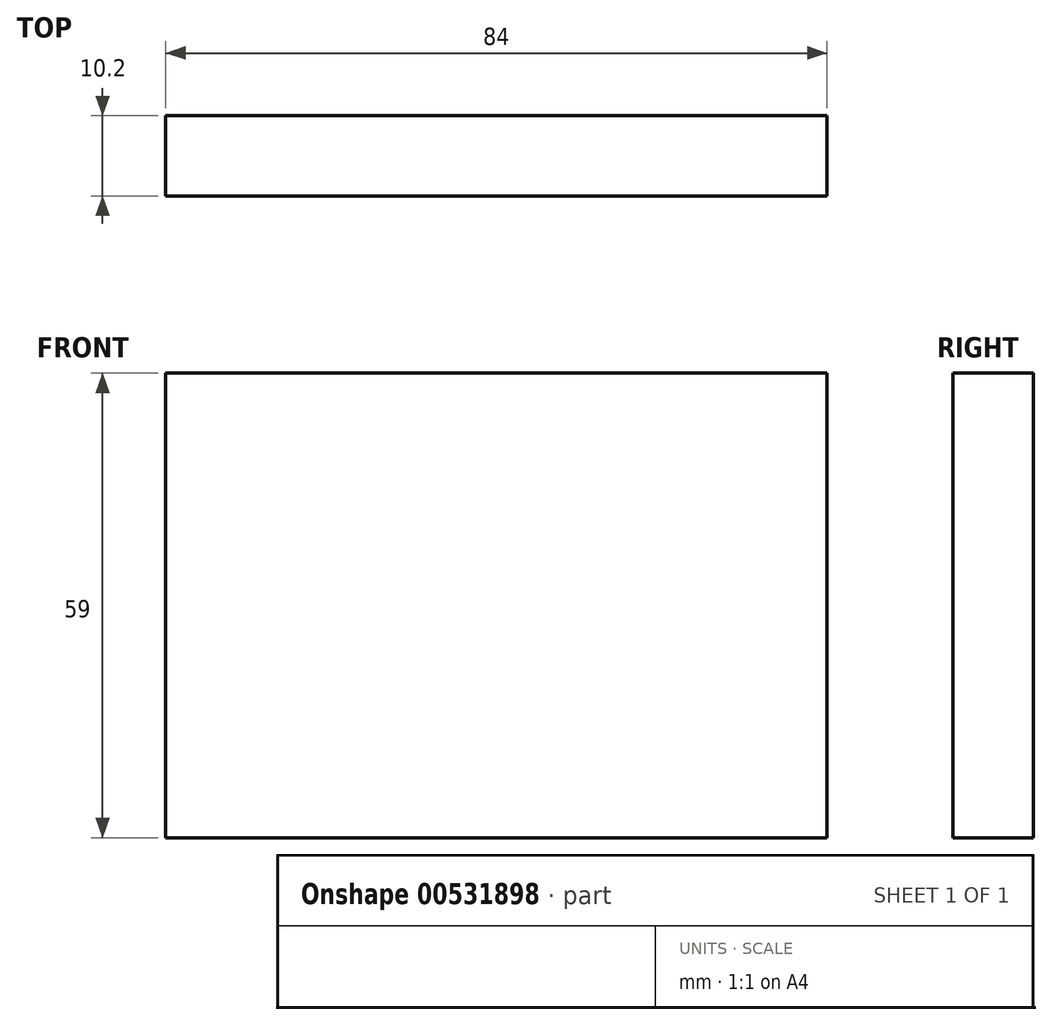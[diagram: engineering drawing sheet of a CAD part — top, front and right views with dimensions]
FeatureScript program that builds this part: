
annotation { "Feature Type Name" : "Feature", "Feature Type Description" : "" }
export const myFeature = defineFeature(function(context is Context, id is Id, definition is map)
    precondition{}
    {
        {
            var Q0;
            Q0=qCreatedBy(makeId("Front.planeOp"),FACE);
            var sketch = newSketch(context, id + "F0", { "sketchPlane" : qUnion([Q0])});
            skLineSegment(sketch, "E0.bottom", {"start": v(42, 29.5) * mm, "end": v(-42, 29.5) * mm});
            skLineSegment(sketch, "E0.top", {"start": v(42, -29.5) * mm, "end": v(-42, -29.5) * mm});
            skLineSegment(sketch, "E0.left", {"start": v(42, 29.5) * mm, "end": v(42, -29.5) * mm});
            skLineSegment(sketch, "E0.right", {"start": v(-42, 29.5) * mm, "end": v(-42, -29.5) * mm});
            skPoint(sketch, "E0.middle", {"position": v(0, 0) * mm});
            skSolve(sketch);
        }
        {
            var Q0;
            Q0=qSketchRegion(id+"F0",true);
            extrude(context, id + "F1", {"entities" : qUnion([Q0]), "depth" : 10.2 * mm, "offsetDistance" : 25 * mm});
        }
    });
